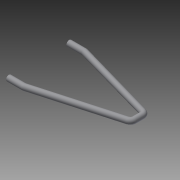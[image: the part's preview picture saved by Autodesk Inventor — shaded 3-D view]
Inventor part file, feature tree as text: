
AUTODESK INVENTOR PART (.ipt)
format: ipt  version: 2014 (Build 180170000, 170)  size: 110,592 bytes
history: native  units: in
note: dims shown in document units (in); Inventor stores cm internally (conversion verified against a paired STEP export)
features: sketch x2, sweep x1
ambient origin geometry x8: Origin, YZ Plane, XZ Plane, XY Plane, X Axis, Y Axis, Z Axis, Center Point
bodies: Solid1 (feature_tree)
feature tree (3):
  sweep  "Sweep1"
  sketch  "Sketch1"  dims[d0=0.375in d1=0.125in]
  sketch  "Sketch2"  dims[d2=0.25in d3=0.25in d5=0.25in d6=5.568in d8=2.0in d9=1.0in d10=0.0in]
